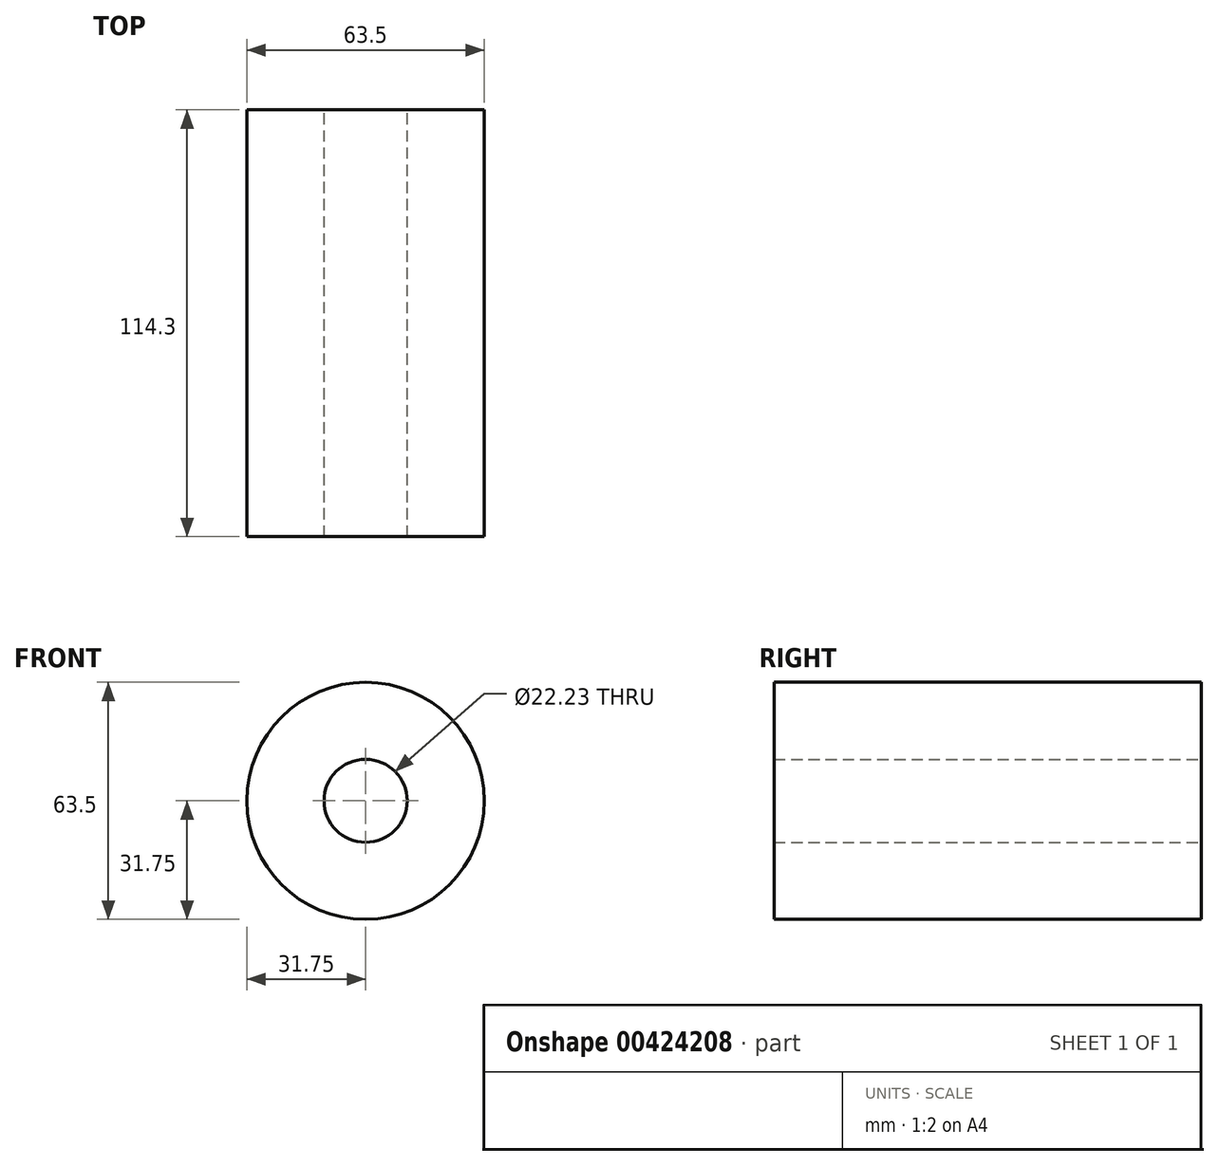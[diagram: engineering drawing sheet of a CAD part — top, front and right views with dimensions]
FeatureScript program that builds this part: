
annotation { "Feature Type Name" : "Feature", "Feature Type Description" : "" }
export const myFeature = defineFeature(function(context is Context, id is Id, definition is map)
    precondition{}
    {
        {
            var Q0;
            Q0=qCreatedBy(makeId("Front.planeOp"),FACE);
            var sketch = newSketch(context, id + "F0", { "sketchPlane" : qUnion([Q0])});
            skCircle(sketch, "E0", {"center": v(0, 0) * mm, "radius": 11.11 * mm});
            skCircle(sketch, "E1", {"center": v(0, 0) * mm, "radius": 31.75 * mm});
            skSolve(sketch);
        }
        {
            var Q0;
            Q0=makeQuery(id+"F0.imprint","IMPRINT",FACE,{"disambiguationData":[TD([[makeQuery(id+"F0.imprint","IMPRINT",EDGE,{"derivedFrom":sQuery(id+"F0.wireOp",EDGE,"E0")}),-1.0]])]});
            extrude(context, id + "F1", {"entities" : qUnion([Q0]), "depth" : 114.3 * mm});
        }
    });
